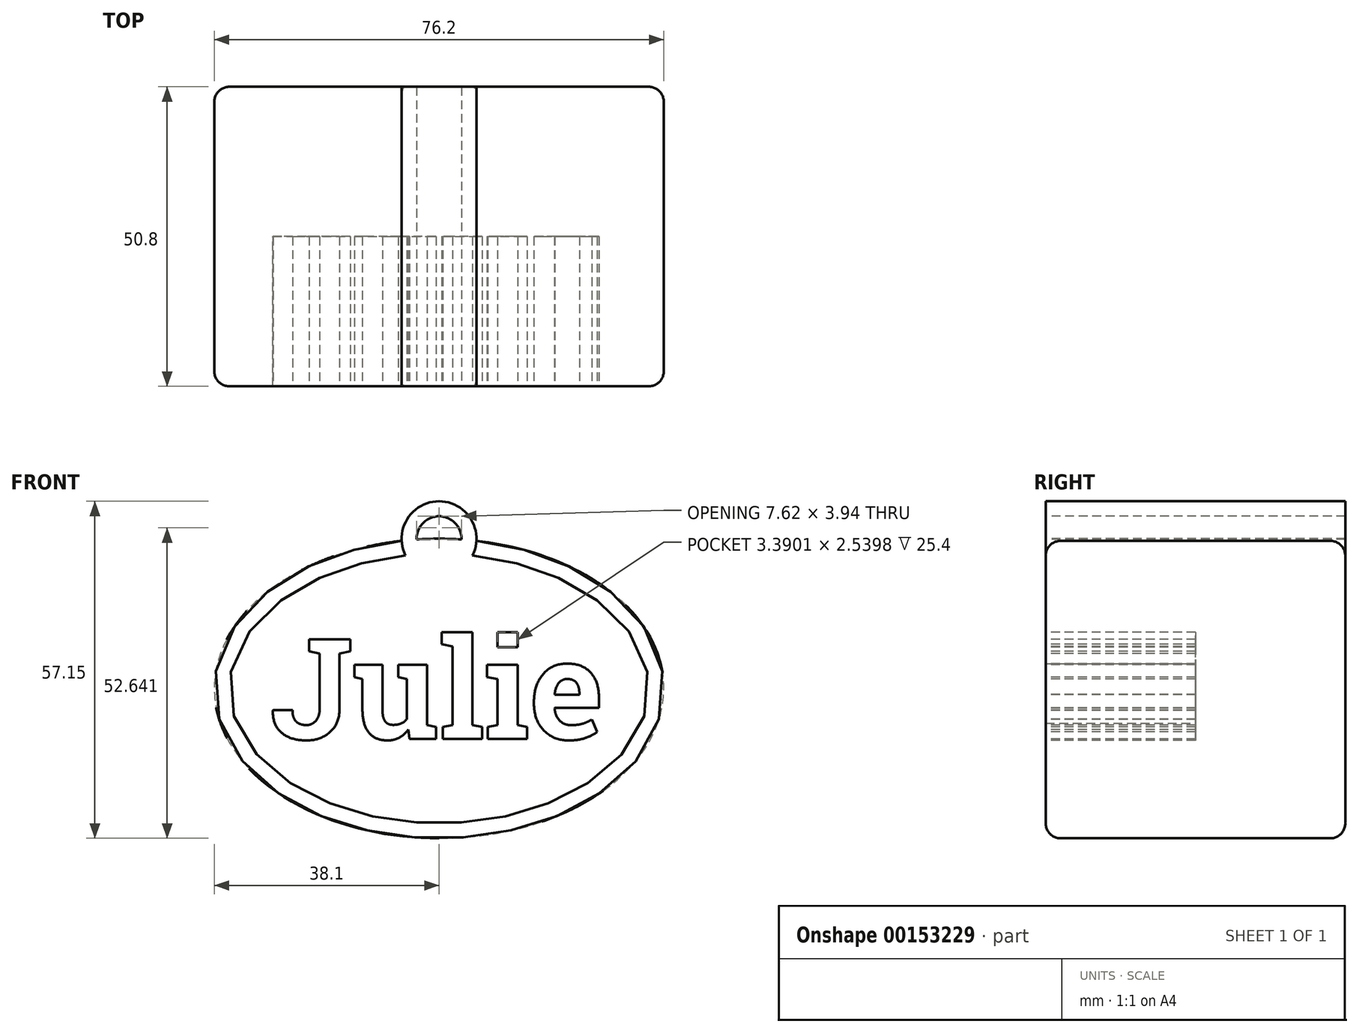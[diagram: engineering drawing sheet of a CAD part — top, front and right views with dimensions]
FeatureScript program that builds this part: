
annotation { "Feature Type Name" : "Feature", "Feature Type Description" : "" }
export const myFeature = defineFeature(function(context is Context, id is Id, definition is map)
    precondition{}
    {
        {
            var Q0;
            Q0=qCreatedBy(makeId("Front.planeOp"),FACE);
            var sketch = newSketch(context, id + "F0", { "sketchPlane" : qUnion([Q0])});
            skEllipse(sketch, "E0", {"center": v(0, 0) * mm, "majorRadius": 38.1 * mm, "minorRadius": 25.4 * mm, "majorAxis": v(1, 0)});
            skSolve(sketch);
        }
        {
            assignVariable(context, id + "F1", {"name" : "nametag_height", "anyValue" : 50.8 * mm});
        }
        {
            var Q0;
            Q0=makeQuery(id+"F0.imprint","IMPRINT",FACE,{"disambiguationData":[TD([[makeQuery(id+"F0.imprint","IMPRINT",EDGE,{"derivedFrom":sQuery(id+"F0.wireOp",EDGE,"E0")}),1.0]])]});
            extrude(context, id + "F2", {"entities" : qUnion([Q0]), "depth" : getVariable(context, 'nametag_height')});
        }
        {
            var Q0;
            Q0=makeQuery(id+"F2.opExtrude","CAP_FACE",FACE,{"disambiguationData":[OSD([sQuery(id+"F0.wireOp",EDGE,"E0")])],"isStart":false});
            var sketch = newSketch(context, id + "F3", { "sketchPlane" : qUnion([Q0])});
            skText(sketch, "E1", { "text": "Julie", "fontName": "RobotoSlab-Bold.ttf"});
            skPoint(sketch, "E2.0", {"position": v(0, 0) * mm});
            const initialGuessF3  = {"E1": [-0.02858, -0.00856, 1, 0, 0.01711]};
            skSetInitialGuess(sketch, initialGuessF3);
            skSolve(sketch);
        }
        {
            var Q0;
            Q0 = qSketchRegion(id + "F3", true);
            extrude(context, id + "F4", {"entities" : qUnion([Q0]), "operationType" : NewBodyOperationType.REMOVE, "oppositeDirection" : true, "depth" : getVariable(context, 'nametag_height') / 2});
        }
        {
            var Q0;
            {var subQ0=sQuery(id+"F0.wireOp",EDGE,"E0");Q0=makeQuery(id+"F4.boolean.opBoolean","SPLIT",FACE,{"disambiguationData":[TD([makeQuery(id+"F2.opExtrude","SWEPT_FACE",FACE,{"disambiguationData":[OSD([subQ0])]})])],"derivedFrom":makeQuery(id+"F2.opExtrude","CAP_FACE",FACE,{"disambiguationData":[OSD([subQ0])],"isStart":false})});}
            var sketch = newSketch(context, id + "F5", { "sketchPlane" : qUnion([Q0])});
            skCircle(sketch, "E3", {"center": v(0, 25.4) * mm, "radius": 3.81 * mm});
            skCircle(sketch, "E4", {"center": v(0, 25.4) * mm, "radius": 6.35 * mm});
            skSolve(sketch);
        }
        {
            var Q0;
            {var subQ0=sQuery(id+"F5.wireOp",EDGE,"E3");var subQ1=makeQuery(id+"F2.opExtrude","CAP_EDGE",EDGE,{"disambiguationData":[OSD([sQuery(id+"F0.wireOp",EDGE,"E0")])],"isStart":false});var subQ2=makeQuery(id+"F5.imprint","INTERSECT",VERTEX,{"disambiguationData":[OD(0.0)],"derivedFrom":[subQ1,subQ0]});Q0=makeQuery(id+"F5.imprint","IMPRINT",FACE,{"disambiguationData":[TD([[makeQuery(id+"F5.imprint","IMPRINT",EDGE,{"disambiguationData":[TD([[subQ2,1.0]])],"derivedFrom":subQ0}),-1.0]])]});}
            var Q1;
            Q1=makeQuery(id+"F2.opExtrude","CAP_FACE",FACE,{"disambiguationData":[OSD([sQuery(id+"F0.wireOp",EDGE,"E0")])],"isStart":true});
            extrude(context, id + "F6", {"entities" : qUnion([Q0]), "operationType" : NewBodyOperationType.ADD, "endBound" : BoundingType.UP_TO_SURFACE, "oppositeDirection" : true, "endBoundEntityFace" : qUnion([Q1]), "depth" : 25.4 * mm});
        }
        {
            var Q0;
            {var subQ0=sQuery(id+"F0.wireOp",EDGE,"E0");var subQ1=sQuery(id+"F5.wireOp",EDGE,"E4");Q0=makeQuery(id+"F6.boolean.opBoolean","SPLIT",EDGE,{"disambiguationData":[TD([makeQuery(id+"F6.opExtrude","SWEPT_FACE",FACE,{"disambiguationData":[OSD([subQ1])]})])],"derivedFrom":makeQuery(id+"F2.opExtrude","CAP_EDGE",EDGE,{"disambiguationData":[OSD([subQ0])],"isStart":false})});}
            var Q1;
            {var subQ0=sQuery(id+"F0.wireOp",EDGE,"E0");Q1=makeQuery(id+"F6.boolean.opBoolean","SPLIT",EDGE,{"disambiguationData":[TD([makeQuery(id+"F6.opExtrude","SWEPT_FACE",FACE,{"disambiguationData":[OSD([sQuery(id+"F5.wireOp",EDGE,"E4")])]})])],"derivedFrom":makeQuery(id+"F2.opExtrude","CAP_EDGE",EDGE,{"disambiguationData":[OSD([subQ0])],"isStart":true})});}
            fillet(context, id + "F7", {"entities" : qUnion([Q0, Q1]), "radius" : 2.54 * mm, "tangentPropagation" : true, "allowEdgeOverflow" : false});
        }
    });
